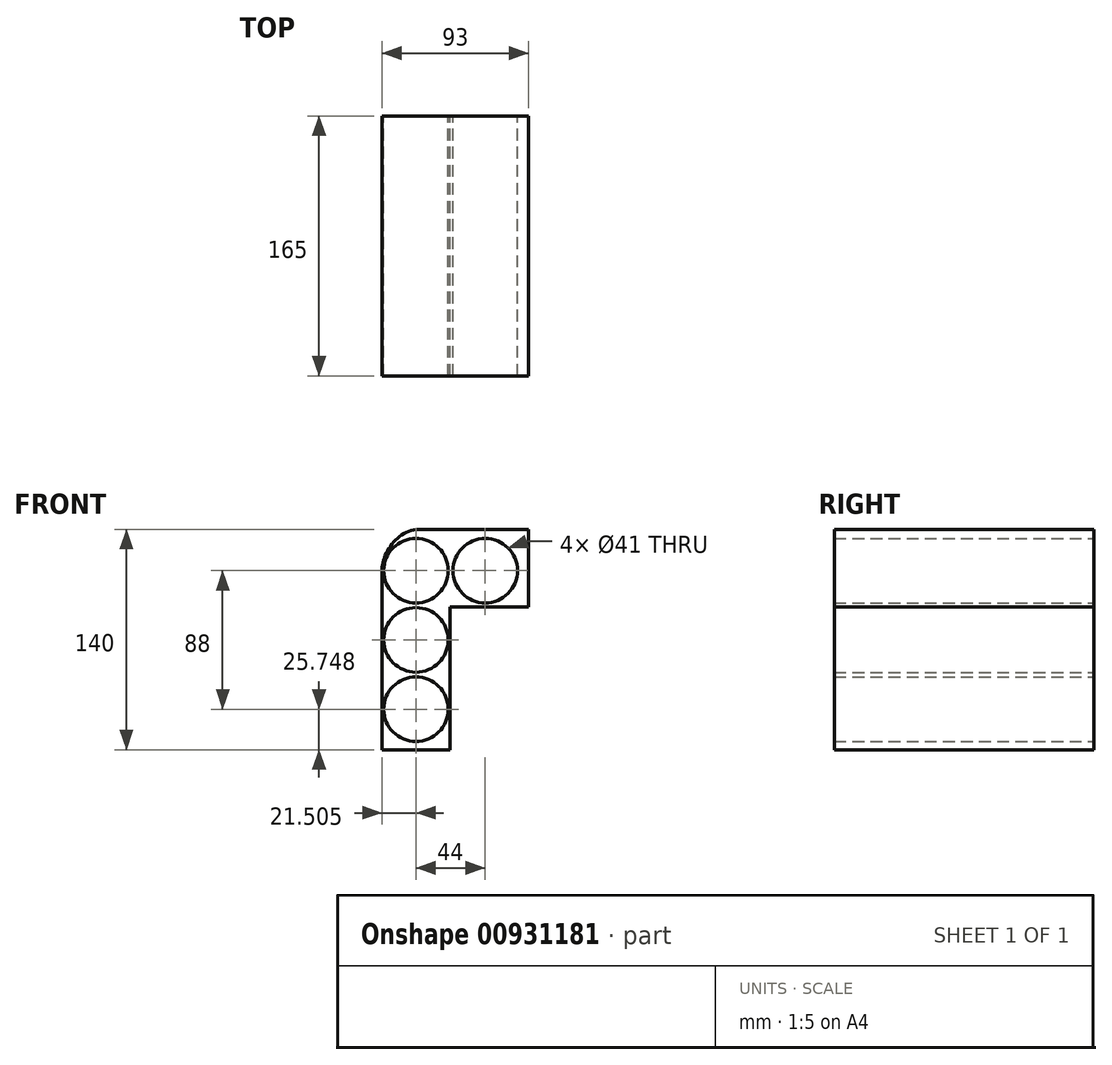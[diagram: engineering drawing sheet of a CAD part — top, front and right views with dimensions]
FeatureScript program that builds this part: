
annotation { "Feature Type Name" : "Feature", "Feature Type Description" : "" }
export const myFeature = defineFeature(function(context is Context, id is Id, definition is map)
    precondition{}
    {
        {
            var Q0;
            Q0=qCreatedBy(makeId("Front.planeOp"),FACE);
            var sketch = newSketch(context, id + "F0", { "sketchPlane" : qUnion([Q0])});
            skCircle(sketch, "E0", {"center": v(-59.76, -29.9) * mm, "radius": 20.5 * mm});
            skCircle(sketch, "E1", {"center": v(-59.76, 14.1) * mm, "radius": 20.5 * mm});
            skLineSegment(sketch, "E2", {"start": v(-59.76, -74.5) * mm, "end": v(-59.76, 74.72) * mm, "construction": true});
            skLineSegment(sketch, "E3", {"start": v(-39.76, -74.77) * mm, "end": v(-39.76, 73.9) * mm, "construction": true});
            skLineSegment(sketch, "E4", {"start": v(-59.76, 58.1) * mm, "end": v(3.24, 58.1) * mm, "construction": true});
            skLineSegment(sketch, "E5", {"start": v(-59.76, -55.65) * mm, "end": v(-38.26, -55.65) * mm});
            skLineSegment(sketch, "E6", {"start": v(-59.76, -55.65) * mm, "end": v(-81.26, -55.65) * mm});
            skLineSegment(sketch, "E7", {"start": v(-81.26, -55.65) * mm, "end": v(-81.26, 58.69) * mm});
            skLineSegment(sketch, "E8", {"start": v(-38.26, -55.65) * mm, "end": v(-38.26, 35.1) * mm});
            skLineSegment(sketch, "E9", {"start": v(-58.02, 84.35) * mm, "end": v(11.74, 84.35) * mm});
            skFitSpline(sketch, "E10", {"points": [v(-81.26, 58.69) * mm, v(-58.02, 84.35) * mm], "startDerivative": vector(0, 32.83) * mm, "endDerivative": vector(38.43, 0) * mm});
            skCircle(sketch, "E11", {"center": v(-59.76, 58.1) * mm, "radius": 20.5 * mm});
            skLineSegment(sketch, "E12", {"start": v(-15.76, 84.35) * mm, "end": v(-15.76, -73.84) * mm, "construction": true});
            skCircle(sketch, "E13", {"center": v(-15.76, 58.1) * mm, "radius": 20.5 * mm});
            skLineSegment(sketch, "E14", {"start": v(-38.26, 35.1) * mm, "end": v(11.74, 35.1) * mm});
            skLineSegment(sketch, "E15", {"start": v(11.74, 35.1) * mm, "end": v(11.74, 84.35) * mm});
            skPoint(sketch, "E16.orphan", {"position": v(26.51, 84.35) * mm});
            skSolve(sketch);
        }
        {
            var Q0;
            Q0=makeQuery(id+"F0.imprint","IMPRINT",FACE,{"disambiguationData":[TD([[makeQuery(id+"F0.imprint","IMPRINT",EDGE,{"derivedFrom":sQuery(id+"F0.wireOp",EDGE,"E0")}),-1.0]])]});
            extrude(context, id + "F1", {"entities" : qUnion([Q0]), "depth" : 165 * mm, "offsetDistance" : 25 * mm});
        }
    });
